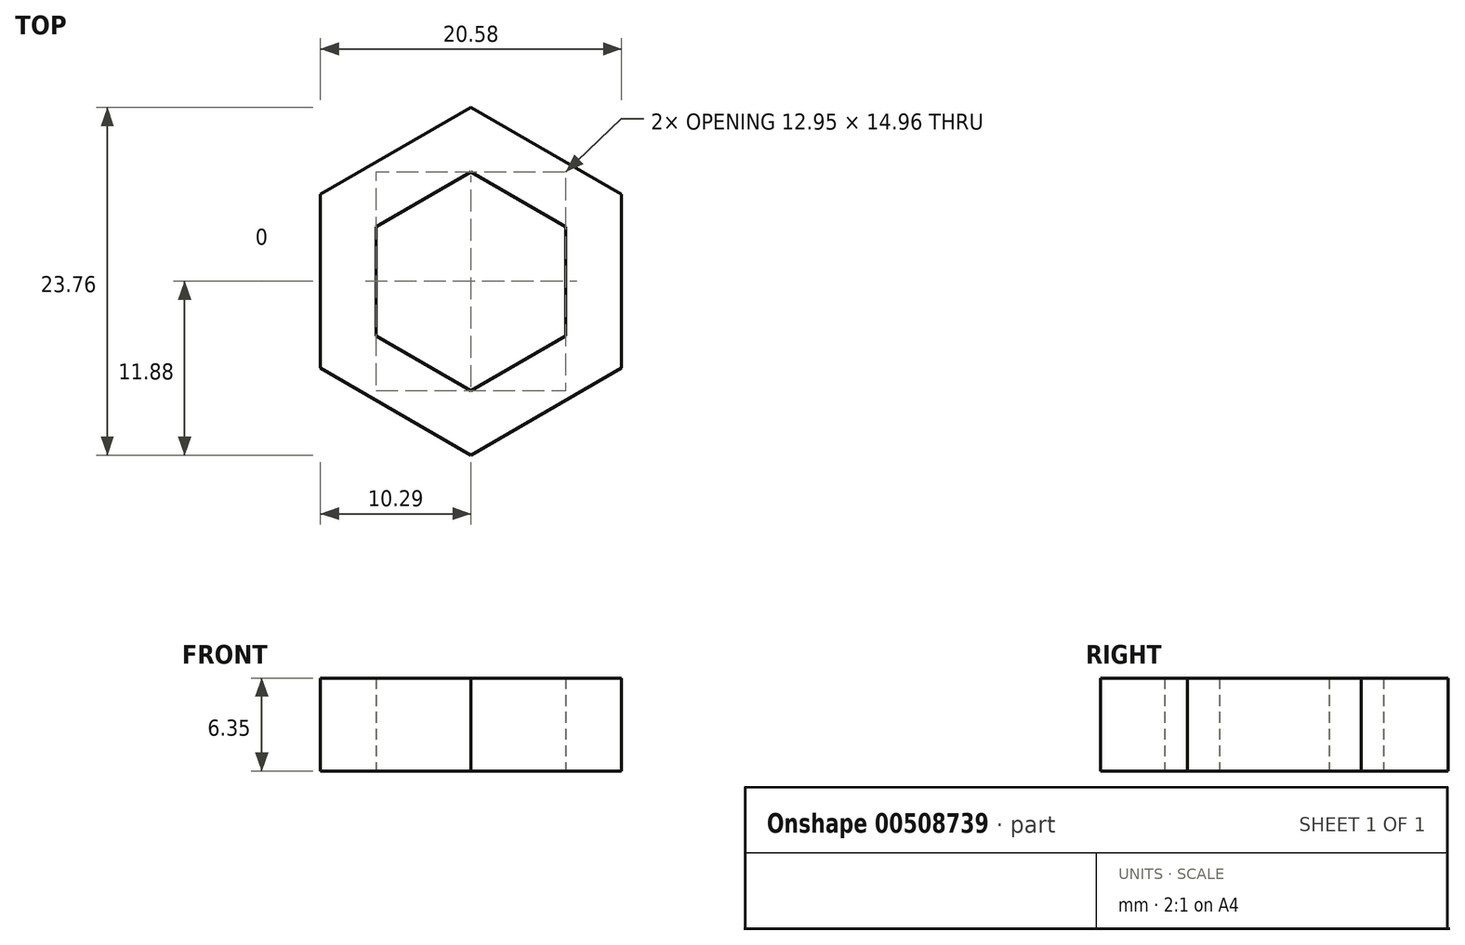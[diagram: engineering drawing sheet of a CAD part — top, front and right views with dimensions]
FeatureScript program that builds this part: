
annotation { "Feature Type Name" : "Feature", "Feature Type Description" : "" }
export const myFeature = defineFeature(function(context is Context, id is Id, definition is map)
    precondition{}
    {
        {
            var Q0;
            Q0=qCreatedBy(makeId("Top.planeOp"),FACE);
            var sketch = newSketch(context, id + "F0", { "sketchPlane" : qUnion([Q0])});
            skCircle(sketch, "E0.cCircle", {"center": v(0, 0) * mm, "radius": 6.48 * mm, "construction": true});
            skLineSegment(sketch, "E0.0", {"start": v(6.48, 3.74) * mm, "end": v(6.48, -3.74) * mm});
            skLineSegment(sketch, "E0.1", {"start": v(6.48, -3.74) * mm, "end": v(0, -7.48) * mm});
            skLineSegment(sketch, "E0.2", {"start": v(0, -7.48) * mm, "end": v(-6.48, -3.74) * mm});
            skLineSegment(sketch, "E0.3", {"start": v(-6.48, -3.74) * mm, "end": v(-6.48, 3.74) * mm});
            skLineSegment(sketch, "E0.4", {"start": v(-6.48, 3.74) * mm, "end": v(0, 7.48) * mm});
            skLineSegment(sketch, "E0.5", {"start": v(0, 7.48) * mm, "end": v(6.48, 3.74) * mm});
            skPoint(sketch, "E0.0.midPoint", {"position": v(6.48, 0) * mm});
            skLineSegment(sketch, "E1.0", {"start": v(-10.29, 5.94) * mm, "end": v(0, 11.88) * mm});
            skLineSegment(sketch, "E1.1", {"start": v(10.29, 5.94) * mm, "end": v(10.29, -5.94) * mm});
            skLineSegment(sketch, "E1.2", {"start": v(10.29, -5.94) * mm, "end": v(0, -11.88) * mm});
            skLineSegment(sketch, "E1.3", {"start": v(0, 11.88) * mm, "end": v(10.29, 5.94) * mm});
            skLineSegment(sketch, "E1.4", {"start": v(0, -11.88) * mm, "end": v(-10.29, -5.94) * mm});
            skLineSegment(sketch, "E1.5", {"start": v(-10.29, -5.94) * mm, "end": v(-10.29, 5.94) * mm});
            skSolve(sketch);
        }
        {
            var Q0;
            Q0=makeQuery(id+"F0.imprint","IMPRINT",FACE,{"disambiguationData":[TD([[makeQuery(id+"F0.imprint","IMPRINT",EDGE,{"derivedFrom":sQuery(id+"F0.wireOp",EDGE,"E0.0")}),1.0]])]});
            extrude(context, id + "F1", {"entities" : qUnion([Q0]), "depth" : 6.35 * mm});
        }
    });
